# Revit family: FL-1
name_source: partatom
category: Lighting Fixtures
revit_build: Autodesk Revit 2014 (Build: 20130308_1515(x64)
units: mm (PartAtom-declared; Revit-internal decimal feet)

## types (12) — shared parameters
Apparent Load = 0 VA
Color Filter = 16777215
Default Elevation = 48 "
Description = FL-1 High Power Floodlight
Dimming Lamp Color Temperature Shift = <None>
Glass = Hubbell - Glass
Lamp = LED
Manufacturer = Beacon Lighting
Model = FL-1
Photometric Web File = FL-1-12L-25-3K7-2X2.ies
Pivot Angle = 135.00°
Product Documentation Link = https://hubbellcdn.com
Product Page URL = https://www.hubbell.com
Tilt Angle = 0.00°
URL = https://www.hubbell.com
Visor Option = FL-1
Voltage = 120-277V
zz Angle 1 = 135.00°

## per-type parameters (varying)
| type | Product Material | Watt |
| Basic Black Textured | Paint - Hubbell - Basic Black Textured | 25 W |
| Gray Smooth | Paint - Hubbell - Gray Smooth | 30 W |
| Black Matte Textured | Paint - Hubbell - Black Matte Textured | 30 W |
| Bronze Textured | Paint - Hubbell - Bronze Textured | 30 W |
| Dark Bronze Textured | Paint - Hubbell - Dark Bronze Textured | 25 W |
| Dark Platinum Smooth | Paint - Hubbell - Dark Platinum Smooth | 30 W |
| Green Textured | Paint - Hubbell - Green Textured | 30 W |
| Metallic Bronze Textured | Paint - Hubbell - Metallic Bronze Textured | 30 W |
| Metallic Silver Textured | Paint - Hubbell - Metallic Silver Textured | 30 W |
| Metallic Titanium Textured | Paint - Hubbell - Metallic Titanium Textured | 30 W |
| Old World Iron | Paint - Hubbell - Old World Iron | 30 W |
| White Texture | Paint - Hubbell - White Texture | 30 W |

## geometry (parser evidence)
native form markers: Sweep x5
no freeform markers — native parametric forms only
